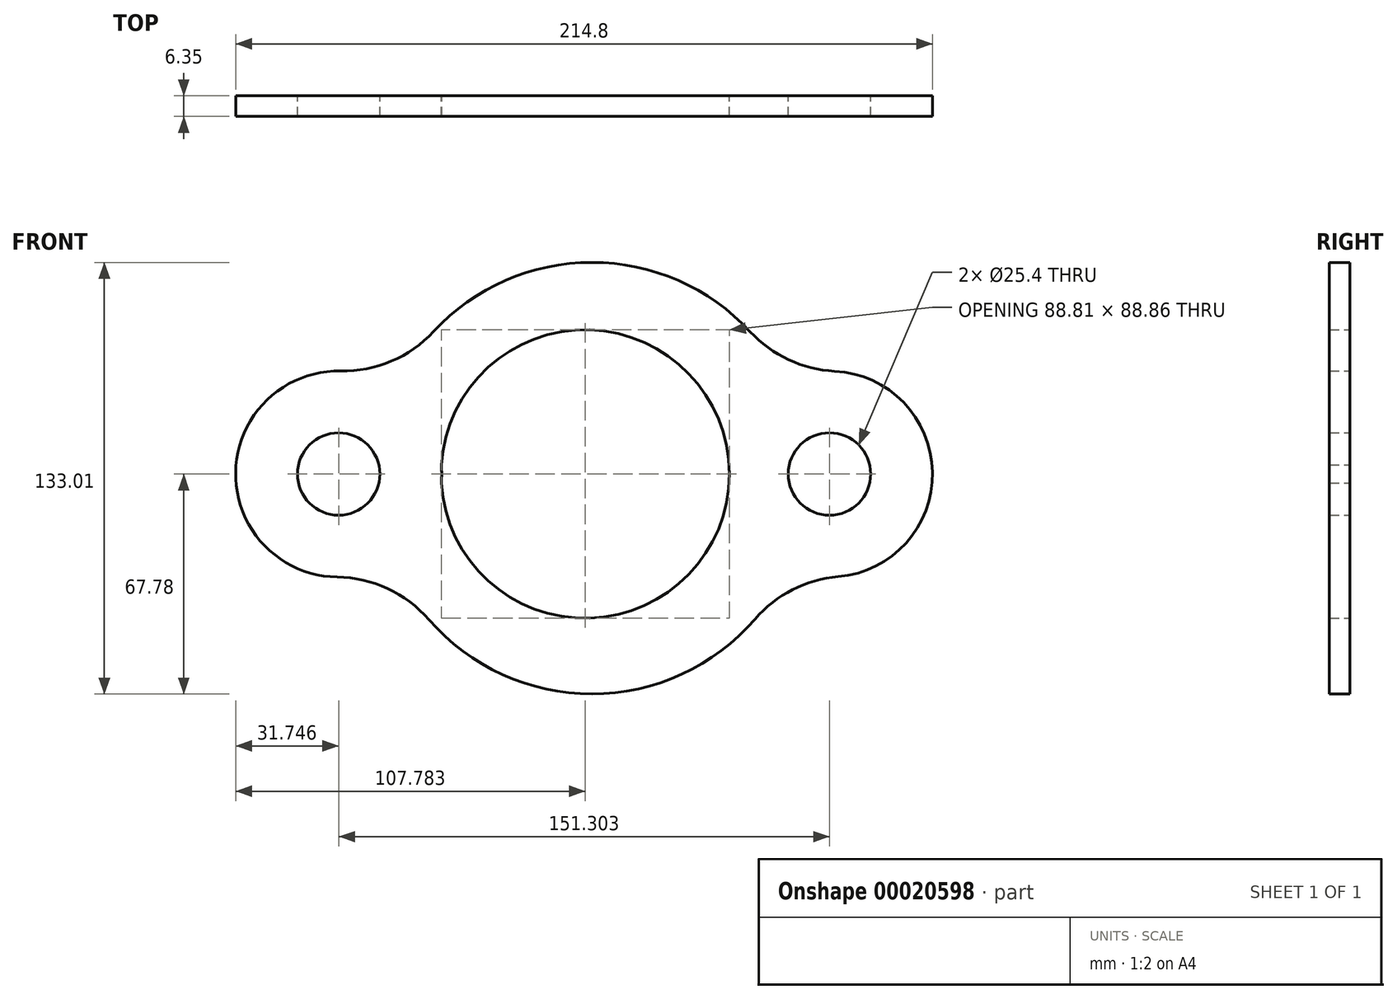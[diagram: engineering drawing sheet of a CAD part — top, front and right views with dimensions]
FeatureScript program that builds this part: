
annotation { "Feature Type Name" : "Feature", "Feature Type Description" : "" }
export const myFeature = defineFeature(function(context is Context, id is Id, definition is map)
    precondition{}
    {
        {
            var Q0;
            Q0=qCreatedBy(makeId("Front.planeOp"),FACE);
            var sketch = newSketch(context, id + "F0", { "sketchPlane" : qUnion([Q0])});
            skArc(sketch, "E0", {"start": v(-44.36, -2.76) * mm, "mid": v(44.45, 0) * mm, "end": v(-44.36, 2.76) * mm});
            skArc(sketch, "E1", {"start": v(-44.36, -2.76) * mm, "mid": v(-44.24, 0) * mm, "end": v(-44.36, 2.76) * mm});
            skCircle(sketch, "E2", {"center": v(-76, 0) * mm, "radius": 12.7 * mm});
            skCircle(sketch, "E3", {"center": v(75.3, 0) * mm, "radius": 12.7 * mm});
            skArc(sketch, "E4", {"start": v(78.01, -31.63) * mm, "mid": v(107.05, 0.55) * mm, "end": v(76.9, 31.7) * mm});
            skArc(sketch, "E5.trimOffspring", {"start": v(-48.18, -44.87) * mm, "mid": v(2.15, -67.78) * mm, "end": v(52.4, -44.71) * mm});
            skLineSegment(sketch, "E6.trimOffspring", {"start": v(44.08, 5.72) * mm, "end": v(44.08, 5.72) * mm});
            skArc(sketch, "E7.trimOffspring", {"start": v(50.86, 43.89) * mm, "mid": v(2.08, 65.23) * mm, "end": v(-46.73, 43.94) * mm});
            skArc(sketch, "E8.trimOffspring", {"start": v(-75.4, 31.74) * mm, "mid": v(-107.74, 0.52) * mm, "end": v(-76.43, -31.75) * mm});
            skPoint(sketch, "E9.visualSharp", {"position": v(-58.41, 26.44) * mm});
            skArc(sketch, "E9.filletArc", {"start": v(-75.4, 31.74) * mm, "mid": v(-59.76, 34.78) * mm, "end": v(-46.73, 43.94) * mm});
            skPoint(sketch, "E10.visualSharp", {"position": v(61.47, 28.58) * mm});
            skArc(sketch, "E10.filletArc", {"start": v(50.86, 43.89) * mm, "mid": v(62.7, 35.25) * mm, "end": v(76.9, 31.7) * mm});
            skPoint(sketch, "E11.visualSharp", {"position": v(62.48, -29.04) * mm});
            skArc(sketch, "E11.filletArc", {"start": v(78.01, -31.63) * mm, "mid": v(63.93, -35.66) * mm, "end": v(52.4, -44.71) * mm});
            skPoint(sketch, "E12.visualSharp", {"position": v(-59.29, -27) * mm});
            skArc(sketch, "E12.filletArc", {"start": v(-48.18, -44.87) * mm, "mid": v(-60.9, -35.29) * mm, "end": v(-76.43, -31.75) * mm});
            skSolve(sketch);
        }
        {
            var Q0;
            Q0 = qSketchRegion(id + "F0", true);
            extrude(context, id + "F1", {"entities" : qUnion([Q0]), "depth" : 6.35 * mm});
        }
    });
